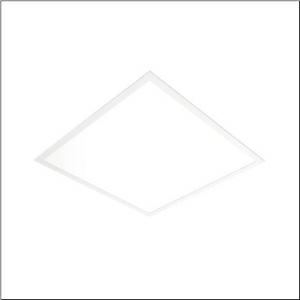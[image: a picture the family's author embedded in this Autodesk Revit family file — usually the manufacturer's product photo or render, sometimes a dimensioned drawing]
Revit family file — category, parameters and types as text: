
# Revit family: apollon_41_51mh12wm2m43
name_source: partatom
category: Lighting Fixtures
units: mm (PartAtom-declared; Revit-internal decimal feet)

## family parameters
Cut with Voids When Loaded = No
Host = Face
Light Source = No
Part Type = Normal
Room Calculation Point = No
Round Connector Dimension = Use Diameter
Shared = No

## types (1)
- --- (1 x LED, 4380 lm, 35 W, 4000K)
    Apparent Load = 35 VA
    CIE Flux Codes = 61 87 97 100 100
    Color Rendering = 80
    Color Temperature = 4000K
    Default Elevation = 1800 mm
    Description = Apollon 41, office luminaire, primary optical cover: prismatic diffuser, of PS, light emission: direct distribution, primary light characteristic: symmetric, installation type: lay-in mounting, LED, rated luminous flux: 4.375lm, luminous efficacy: 125lm/W, light colour: 830/840, colour temperature: 3000/4000K, control gear: ON/OFF Multilumen, with terminal, 3-pole, mains connection: 220..240V, AC, 50/60Hz, rated input power: 35W, suitable for self-contained emergency lighting element 58DB00B013A with integrated self-test function according to EN 60598-2-22, housing, of aluminium section, traffic white (RAL 9016), module: M600, length: 595mm, width: 595mm, height: 60mm, recess depth: 180mm, housing upper side, of sheet steel, protection rating (complete): IP20, protection rating (lamp compartment, on room side): IP40, insulation class (complete): insulation class II (safety insulation), certification: CE, ENEC, impact resistance: IK03, permissible operating ambient temperature: -25..+40°C, packaging unit: 1 piece
    Height = 0 mm  [stored 0 ft]
    Lamp = 1 x LED
    Lamp Light Flux = 4380 lm
    Lamp Power = 35 W
    Lamp count = 1
    Length = 600 mm
    Luminous efficacy = 125 lm/W
    Manufacturer = Siteco
    ModVariant = No
    Model = 51MH12WM2M43
    Mounting Place = Ceiling
    Mounting Type = Recessed
    Number of Poles = 1
    OnlyDefault = Yes
    Power Factor = 1
    Product Name = Apollon 41
    Product group = office luminaire | ceiling recessed
    ProductGroupID = 400
    Protection Class = Protection class II
    Protection Degree = IP 20
    RLX_Detail_Level = 1
    RLX_Emergency_Light_Flux = 0 lm
    RLX_Emergency_Type = 0
    RLX_Emergency_Type_DB = No
    RlxData = <blob elided: 13725 chars, md5=37ad91e9>
    Socket = socket
    Standby Power = 0 W
    System Light Flux = 4380 lm
    System Power = 35 W
    Type Comments = factory setting: luminous flux: 100 % | (ON | ON) | 900 mA
    Type Image = l_1291024.jpg
    URL = http://relux.com
    VarID = @adj_033381
    Voltage = 0 V
    Weight = 0.00 kg
    Width = 600 mm

note: [stored X ft] marks values corroborated as IEEE doubles in the binary element streams (Revit-internal decimal feet)

## geometry (parser evidence)
native form markers: Sweep x13
no freeform markers — native parametric forms only
